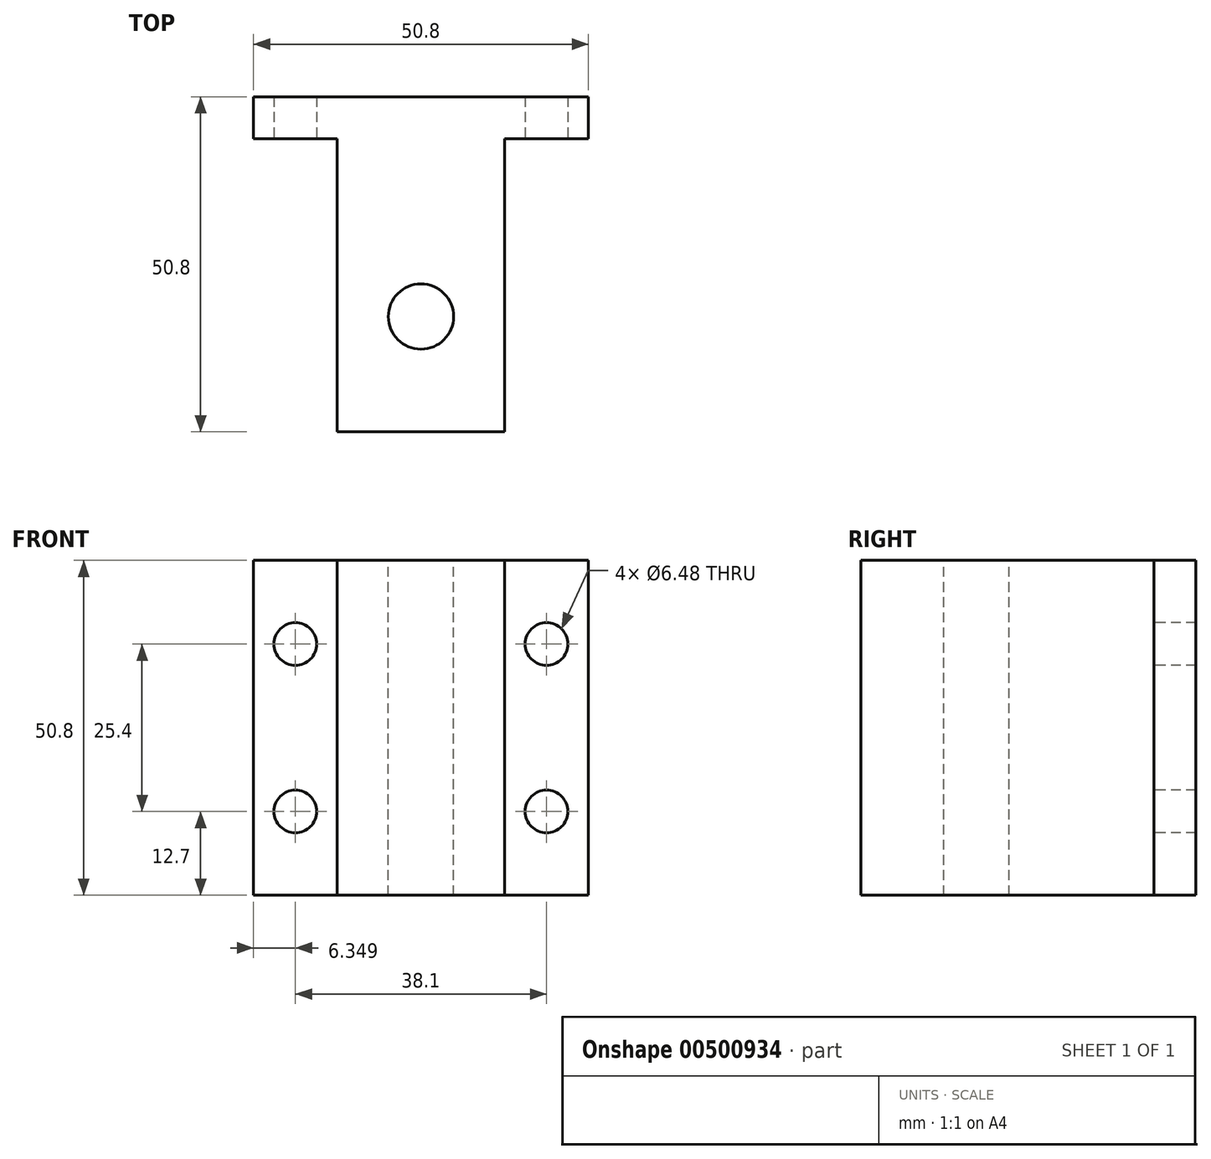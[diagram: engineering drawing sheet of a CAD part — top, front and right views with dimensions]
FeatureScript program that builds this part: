
annotation { "Feature Type Name" : "Feature", "Feature Type Description" : "" }
export const myFeature = defineFeature(function(context is Context, id is Id, definition is map)
    precondition{}
    {
        {
            var Q0;
            Q0=qCreatedBy(makeId("Top.planeOp"),FACE);
            var sketch = newSketch(context, id + "F0", { "sketchPlane" : qUnion([Q0])});
            skLineSegment(sketch, "E0", {"start": v(-30.8, 0) * mm, "end": v(20, 0) * mm});
            skLineSegment(sketch, "E1", {"start": v(20, 0) * mm, "end": v(20, -6.35) * mm});
            skLineSegment(sketch, "E2", {"start": v(20, -6.35) * mm, "end": v(7.3, -6.35) * mm});
            skLineSegment(sketch, "E3", {"start": v(7.3, -6.35) * mm, "end": v(7.3, -50.8) * mm});
            skLineSegment(sketch, "E4", {"start": v(7.3, -50.8) * mm, "end": v(-18.1, -50.8) * mm});
            skLineSegment(sketch, "E5", {"start": v(-18.1, -50.8) * mm, "end": v(-18.1, -6.35) * mm});
            skLineSegment(sketch, "E6", {"start": v(-18.1, -6.35) * mm, "end": v(-30.8, -6.35) * mm});
            skLineSegment(sketch, "E7", {"start": v(-30.8, -6.35) * mm, "end": v(-30.8, 0) * mm});
            skSolve(sketch);
        }
        {
            var Q0;
            Q0=makeQuery(id+"F0.imprint","IMPRINT",FACE,{"disambiguationData":[TD([[makeQuery(id+"F0.imprint","IMPRINT",EDGE,{"derivedFrom":sQuery(id+"F0.wireOp",EDGE,"E0")}),-1.0]])]});
            extrude(context, id + "F1", {"entities" : qUnion([Q0]), "depth" : 50.8 * mm, "offsetDistance" : 25.4 * mm});
        }
        {
            var Q0;
            Q0=makeQuery(id+"F1.opExtrude","CAP_FACE",FACE,{"disambiguationData":[OSD([sQuery(id+"F0.wireOp",EDGE,"E0"),sQuery(id+"F0.wireOp",EDGE,"E1"),sQuery(id+"F0.wireOp",EDGE,"E2"),sQuery(id+"F0.wireOp",EDGE,"E3"),sQuery(id+"F0.wireOp",EDGE,"E4"),sQuery(id+"F0.wireOp",EDGE,"E5"),sQuery(id+"F0.wireOp",EDGE,"E6"),sQuery(id+"F0.wireOp",EDGE,"E7")])],"isStart":false});
            var sketch = newSketch(context, id + "F2", { "sketchPlane" : qUnion([Q0])});
            skCircle(sketch, "E8", {"center": v(-5.4, -33.32) * mm, "radius": 4.95 * mm});
            skSolve(sketch);
        }
        {
            var Q0;
            Q0=makeQuery(id+"F2.imprint","IMPRINT",FACE,{"disambiguationData":[TD([[makeQuery(id+"F2.imprint","IMPRINT",EDGE,{"derivedFrom":sQuery(id+"F2.wireOp",EDGE,"E8")}),1.0]])]});
            extrude(context, id + "F3", {"entities" : qUnion([Q0]), "operationType" : NewBodyOperationType.REMOVE, "oppositeDirection" : true, "depth" : 50.8 * mm, "offsetDistance" : 25.4 * mm});
        }
        {
            var Q0;
            Q0=makeQuery(id+"F1.opExtrude","SWEPT_FACE",FACE,{"disambiguationData":[OSD([sQuery(id+"F0.wireOp",EDGE,"E2")])]});
            var sketch = newSketch(context, id + "F4", { "sketchPlane" : qUnion([Q0])});
            skCircle(sketch, "E9", {"center": v(13.65, 38.1) * mm, "radius": 3.24 * mm});
            skCircle(sketch, "E10", {"center": v(13.65, 12.7) * mm, "radius": 3.24 * mm});
            skCircle(sketch, "E11", {"center": v(-24.45, 12.7) * mm, "radius": 3.24 * mm});
            skCircle(sketch, "E12", {"center": v(-24.45, 38.1) * mm, "radius": 3.24 * mm});
            skSolve(sketch);
        }
        {
            var Q0;
            Q0=makeQuery(id+"F4.imprint","IMPRINT",FACE,{"disambiguationData":[TD([[makeQuery(id+"F4.imprint","IMPRINT",EDGE,{"derivedFrom":sQuery(id+"F4.wireOp",EDGE,"E12")}),1.0]])]});
            var Q1;
            Q1=makeQuery(id+"F4.imprint","IMPRINT",FACE,{"disambiguationData":[TD([[makeQuery(id+"F4.imprint","IMPRINT",EDGE,{"derivedFrom":sQuery(id+"F4.wireOp",EDGE,"E11")}),1.0]])]});
            var Q2;
            Q2=makeQuery(id+"F4.imprint","IMPRINT",FACE,{"disambiguationData":[TD([[makeQuery(id+"F4.imprint","IMPRINT",EDGE,{"derivedFrom":sQuery(id+"F4.wireOp",EDGE,"E9")}),1.0]])]});
            var Q3;
            Q3=makeQuery(id+"F4.imprint","IMPRINT",FACE,{"disambiguationData":[TD([[makeQuery(id+"F4.imprint","IMPRINT",EDGE,{"derivedFrom":sQuery(id+"F4.wireOp",EDGE,"E10")}),1.0]])]});
            extrude(context, id + "F5", {"entities" : qUnion([Q0, Q1, Q2, Q3]), "operationType" : NewBodyOperationType.REMOVE, "oppositeDirection" : true, "depth" : 25.4 * mm, "offsetDistance" : 25.4 * mm});
        }
    });
